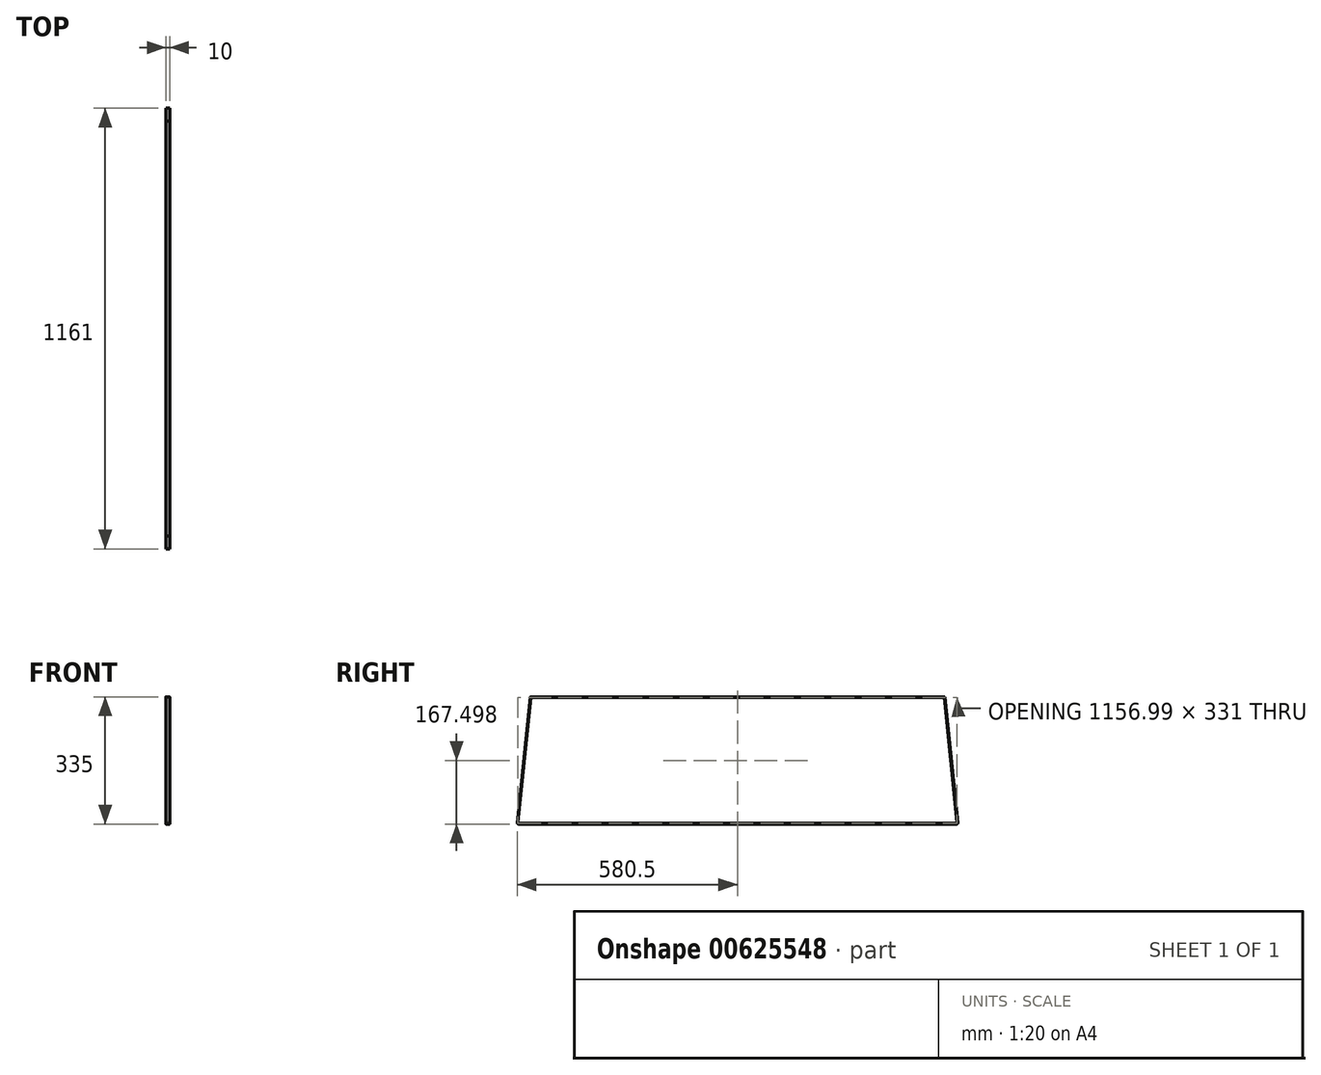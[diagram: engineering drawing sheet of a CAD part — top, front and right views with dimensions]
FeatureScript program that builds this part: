
annotation { "Feature Type Name" : "Feature", "Feature Type Description" : "" }
export const myFeature = defineFeature(function(context is Context, id is Id, definition is map)
    precondition{}
    {
        {
            var Q0;
            Q0=qCreatedBy(makeId("Right.planeOp"),FACE);
            var sketch = newSketch(context, id + "F0", { "sketchPlane" : qUnion([Q0])});
            skLineSegment(sketch, "E0.bottom", {"start": v(-545, 170) * mm, "end": v(0, 170) * mm});
            skLineSegment(sketch, "E0.top", {"start": v(-578, -165) * mm, "end": v(0, -165) * mm});
            skPoint(sketch, "E0.middle", {"position": v(0, 0) * mm});
            skLineSegment(sketch, "E1.bottom", {"start": v(-543, 168) * mm, "end": v(0, 168) * mm});
            skLineSegment(sketch, "E1.top", {"start": v(-576, -163) * mm, "end": v(0, -163) * mm});
            skPoint(sketch, "E2.visualSharp", {"position": v(-554.58, -165) * mm});
            skPoint(sketch, "E3.visualSharp", {"position": v(-560.63, -163) * mm});
            skPoint(sketch, "E4.visualSharp", {"position": v(-546.1, 168) * mm});
            skArc(sketch, "E4.filletArc", {"start": v(-543, 168) * mm, "mid": v(-544.01, 167.78) * mm, "end": v(-544.85, 167.18) * mm});
            skPoint(sketch, "E5.visualSharp", {"position": v(-540.1, 170) * mm});
            skArc(sketch, "E5.filletArc", {"start": v(-545, 170) * mm, "mid": v(-545.8, 169.87) * mm, "end": v(-546.5, 169.5) * mm});
            skPoint(sketch, "E3.filletArc.center.orphan", {"position": v(-575, -173) * mm});
            skPoint(sketch, "E2.filletArc.center.orphan", {"position": v(-577, -175) * mm});
            skPoint(sketch, "E6.visualSharp", {"position": v(-578.66, -163) * mm});
            skArc(sketch, "E6.filletArc", {"start": v(-578.5, -160.35) * mm, "mid": v(-577.82, -162.21) * mm, "end": v(-576, -163) * mm});
            skPoint(sketch, "E7.visualSharp", {"position": v(-580.77, -165) * mm});
            skArc(sketch, "E7.filletArc", {"start": v(-580.49, -162.24) * mm, "mid": v(-579.86, -164.18) * mm, "end": v(-578, -165) * mm});
            skLineSegment(sketch, "E8", {"start": v(-546.5, 169.5) * mm, "end": v(-580.49, -162.24) * mm});
            skLineSegment(sketch, "E9", {"start": v(0, 0) * mm, "end": v(0, 377.6) * mm, "construction": true});
            skPoint(sketch, "E9.endSnap0", {"position": v(0, 165.02) * mm});
            skLineSegment(sketch, "E10", {"start": v(-544.85, 167.18) * mm, "end": v(-578.5, -160.35) * mm});
            skArc(sketch, "E11.MirrorCS", {"start": v(543, 168) * mm, "mid": v(544.01, 167.78) * mm, "end": v(544.85, 167.18) * mm});
            skArc(sketch, "E12.MirrorCS", {"start": v(578.5, -160.35) * mm, "mid": v(577.82, -162.21) * mm, "end": v(576, -163) * mm});
            skArc(sketch, "E13.MirrorCS", {"start": v(545, 170) * mm, "mid": v(545.8, 169.87) * mm, "end": v(546.5, 169.5) * mm});
            skArc(sketch, "E14.MirrorCS", {"start": v(580.49, -162.24) * mm, "mid": v(579.86, -164.18) * mm, "end": v(578, -165) * mm});
            skLineSegment(sketch, "E15.MirrorCS", {"start": v(578, -165) * mm, "end": v(0, -165) * mm});
            skPoint(sketch, "E16.MirrorP", {"position": v(580.77, -165) * mm});
            skLineSegment(sketch, "E17.MirrorCS", {"start": v(544.85, 167.18) * mm, "end": v(578.5, -160.35) * mm});
            skPoint(sketch, "E18.MirrorP", {"position": v(577, -175) * mm});
            skPoint(sketch, "E19.MirrorP", {"position": v(578.66, -163) * mm});
            skLineSegment(sketch, "E20.MirrorCS", {"start": v(543, 168) * mm, "end": v(0, 168) * mm});
            skPoint(sketch, "E21.MirrorP", {"position": v(546.1, 168) * mm});
            skLineSegment(sketch, "E22.MirrorCS", {"start": v(576, -163) * mm, "end": v(0, -163) * mm});
            skLineSegment(sketch, "E23.MirrorCS", {"start": v(545, 170) * mm, "end": v(0, 170) * mm});
            skLineSegment(sketch, "E24.MirrorCS", {"start": v(546.5, 169.5) * mm, "end": v(580.49, -162.24) * mm});
            skPoint(sketch, "E25.MirrorP", {"position": v(554.58, -165) * mm});
            skPoint(sketch, "E26.MirrorP", {"position": v(560.63, -163) * mm});
            skPoint(sketch, "E27.MirrorP", {"position": v(575, -173) * mm});
            skPoint(sketch, "E28.MirrorP", {"position": v(540.1, 170) * mm});
            skSolve(sketch);
        }
        {
            var Q0;
            Q0=makeQuery(id+"F0.imprint","IMPRINT",FACE,{"disambiguationData":[TD([[makeQuery(id+"F0.imprint","IMPRINT",EDGE,{"derivedFrom":sQuery(id+"F0.wireOp",EDGE,"E0.bottom")}),-1.0]])]});
            extrude(context, id + "F1", {"entities" : qUnion([Q0]), "depth" : 10 * mm, "offsetDistance" : 25 * mm});
        }
    });
